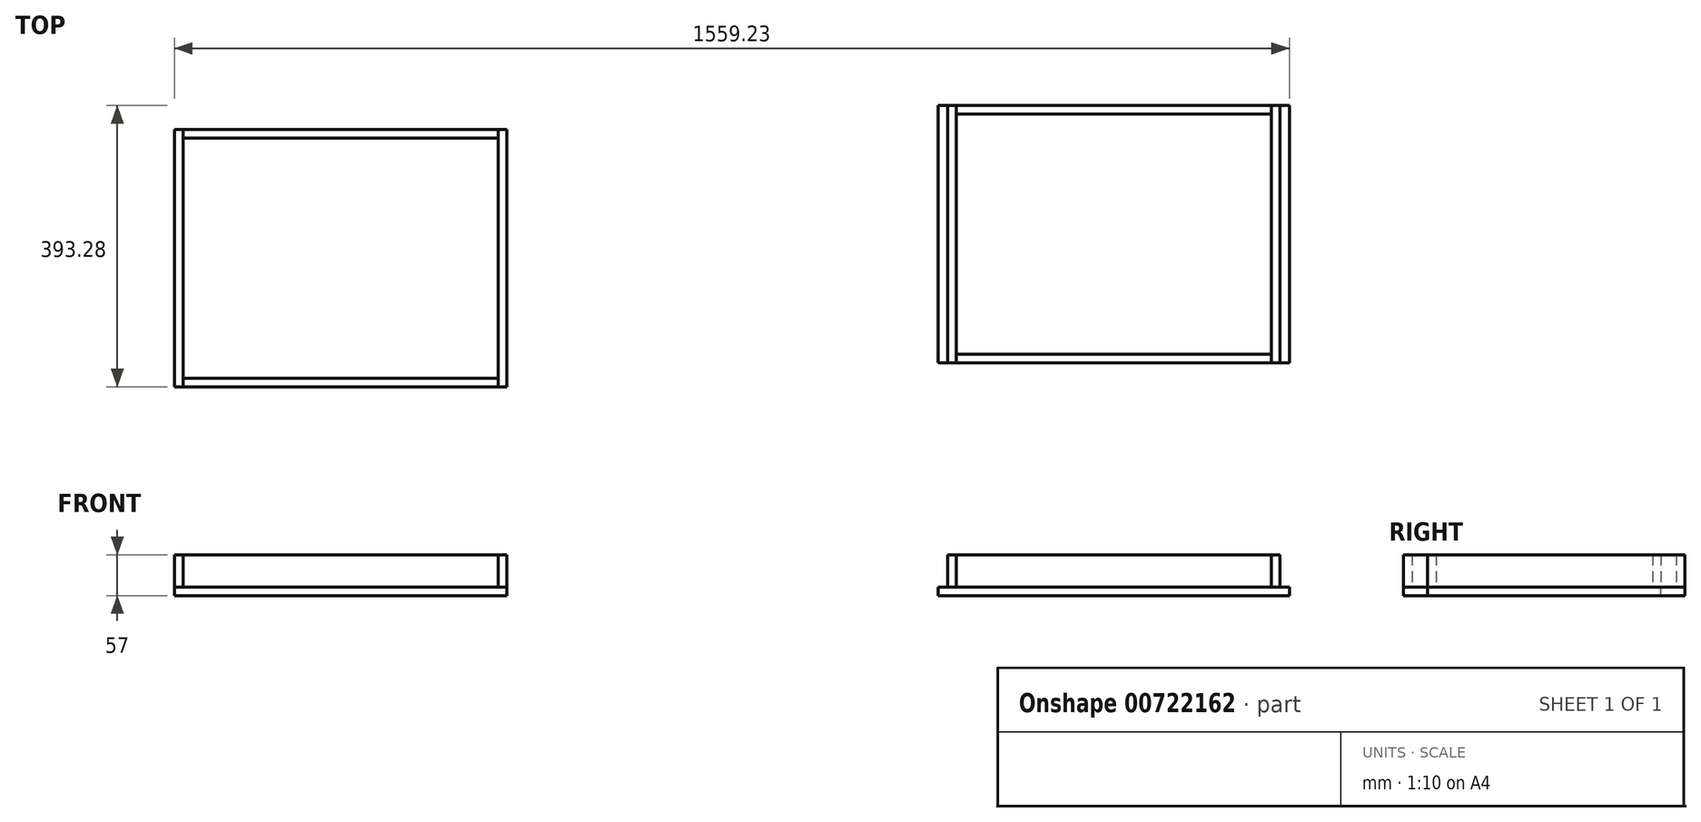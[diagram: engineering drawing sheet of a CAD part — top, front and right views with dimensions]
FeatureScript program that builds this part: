
annotation { "Feature Type Name" : "Feature", "Feature Type Description" : "" }
export const myFeature = defineFeature(function(context is Context, id is Id, definition is map)
    precondition{}
    {
        {
            var Q0;
            Q0=qCreatedBy(makeId("Top.planeOp"),FACE);
            var sketch = newSketch(context, id + "F0", { "sketchPlane" : qUnion([Q0])});
            skLineSegment(sketch, "E0.bottom", {"start": v(-232.5, -180) * mm, "end": v(232.5, -180) * mm});
            skLineSegment(sketch, "E0.top", {"start": v(-232.5, 180) * mm, "end": v(232.5, 180) * mm});
            skLineSegment(sketch, "E0.left", {"start": v(-232.5, -180) * mm, "end": v(-232.5, 180) * mm});
            skLineSegment(sketch, "E0.right", {"start": v(232.5, -180) * mm, "end": v(232.5, 180) * mm});
            skPoint(sketch, "E0.middle", {"position": v(0, 0) * mm});
            skLineSegment(sketch, "E1", {"start": v(-220.5, 180) * mm, "end": v(-220.5, -180) * mm});
            skLineSegment(sketch, "E2", {"start": v(220.5, 180) * mm, "end": v(220.5, -180) * mm});
            skLineSegment(sketch, "E3", {"start": v(-220.5, -168) * mm, "end": v(220.5, -168) * mm});
            skLineSegment(sketch, "E4", {"start": v(-220.5, 168) * mm, "end": v(220.5, 168) * mm});
            skLineSegment(sketch, "E5", {"start": v(-232.5, -180) * mm, "end": v(-245.5, -180) * mm});
            skLineSegment(sketch, "E6", {"start": v(-245.5, -180) * mm, "end": v(-245.5, 180) * mm});
            skLineSegment(sketch, "E7", {"start": v(-245.5, 180) * mm, "end": v(-232.5, 180) * mm});
            skLineSegment(sketch, "E8", {"start": v(232.5, 180) * mm, "end": v(245.5, 180) * mm});
            skLineSegment(sketch, "E9", {"start": v(245.5, 180) * mm, "end": v(245.5, -180) * mm});
            skLineSegment(sketch, "E10", {"start": v(245.5, -180) * mm, "end": v(232.5, -180) * mm});
            skSolve(sketch);
        }
        {
            var Q0;
            Q0 = qSketchRegion(id + "F0", true);
            var Q1;
            {var subQ0=sQuery(id+"F0.wireOp",EDGE,"E3");Q1=makeQuery(id+"F0.imprint","IMPRINT",FACE,{"disambiguationData":[TD([[makeQuery(id+"F0.imprint","IMPRINT",EDGE,{"derivedFrom":subQ0}),1.0]])]});}
            extrude(context, id + "F1", {"entities" : qUnion([Q0, Q1]), "oppositeDirection" : true, "depth" : 12 * mm, "offsetDistance" : 25 * mm});
        }
        {
            var Q0;
            {var subQ0=sQuery(id+"F0.wireOp",EDGE,"E0.left");Q0=makeQuery(id+"F0.imprint","IMPRINT",FACE,{"disambiguationData":[TD([[makeQuery(id+"F0.imprint","IMPRINT",EDGE,{"derivedFrom":subQ0}),-1.0]])]});}
            var Q1;
            {var subQ4=sQuery(id+"F0.wireOp",EDGE,"E0.right");Q1=makeQuery(id+"F0.imprint","IMPRINT",FACE,{"disambiguationData":[TD([[makeQuery(id+"F0.imprint","IMPRINT",EDGE,{"derivedFrom":subQ4}),1.0]])]});}
            extrude(context, id + "F2", {"entities" : qUnion([Q0, Q1]), "depth" : 45 * mm, "offsetDistance" : 25 * mm});
        }
        {
            var Q0;
            {var subQ5=sQuery(id+"F0.wireOp",EDGE,"E4");Q0=makeQuery(id+"F0.imprint","IMPRINT",FACE,{"disambiguationData":[TD([[makeQuery(id+"F0.imprint","IMPRINT",EDGE,{"derivedFrom":subQ5}),1.0]])]});}
            var Q1;
            {var subQ5=sQuery(id+"F0.wireOp",EDGE,"E3");Q1=makeQuery(id+"F0.imprint","IMPRINT",FACE,{"disambiguationData":[TD([[makeQuery(id+"F0.imprint","IMPRINT",EDGE,{"derivedFrom":subQ5}),-1.0]])]});}
            extrude(context, id + "F3", {"entities" : qUnion([Q0, Q1]), "depth" : 45 * mm, "offsetDistance" : 25 * mm});
        }
        {
            var Q0;
            Q0=qCreatedBy(makeId("Top.planeOp"),FACE);
            var sketch = newSketch(context, id + "F4", { "sketchPlane" : qUnion([Q0])});
            skLineSegment(sketch, "E11.bottom", {"start": v(-1313.73, -213.28) * mm, "end": v(-848.73, -213.28) * mm});
            skLineSegment(sketch, "E11.top", {"start": v(-1313.73, 146.72) * mm, "end": v(-848.73, 146.72) * mm});
            skLineSegment(sketch, "E11.left", {"start": v(-1313.73, -213.28) * mm, "end": v(-1313.73, 146.72) * mm});
            skLineSegment(sketch, "E11.right", {"start": v(-848.73, -213.28) * mm, "end": v(-848.73, 146.72) * mm});
            skPoint(sketch, "E11.middle", {"position": v(-1081.23, -33.28) * mm});
            skLineSegment(sketch, "E12", {"start": v(-1301.73, 146.72) * mm, "end": v(-1301.73, -213.28) * mm});
            skLineSegment(sketch, "E13", {"start": v(-860.73, 146.72) * mm, "end": v(-860.73, -213.28) * mm});
            skLineSegment(sketch, "E14", {"start": v(-1301.73, -201.28) * mm, "end": v(-860.73, -201.28) * mm});
            skLineSegment(sketch, "E15", {"start": v(-1301.73, 134.72) * mm, "end": v(-860.73, 134.72) * mm});
            skLineSegment(sketch, "E16", {"start": v(-1313.73, -213.28) * mm, "end": v(-1326.73, -213.28) * mm});
            skLineSegment(sketch, "E17", {"start": v(-1326.73, -213.28) * mm, "end": v(-1326.73, 146.72) * mm});
            skLineSegment(sketch, "E18", {"start": v(-1326.73, 146.72) * mm, "end": v(-1313.73, 146.72) * mm});
            skLineSegment(sketch, "E19", {"start": v(-848.73, 146.72) * mm, "end": v(-835.73, 146.72) * mm});
            skLineSegment(sketch, "E20", {"start": v(-835.73, 146.72) * mm, "end": v(-835.73, -213.28) * mm});
            skLineSegment(sketch, "E21", {"start": v(-835.73, -213.28) * mm, "end": v(-848.73, -213.28) * mm});
            skSolve(sketch);
        }
        {
            var Q0;
            {var subQ5=sQuery(id+"F4.wireOp",EDGE,"E14");Q0=makeQuery(id+"F4.imprint","IMPRINT",FACE,{"disambiguationData":[TD([[makeQuery(id+"F4.imprint","IMPRINT",EDGE,{"derivedFrom":subQ5}),-1.0]])]});}
            var Q1;
            {var subQ5=sQuery(id+"F4.wireOp",EDGE,"E15");Q1=makeQuery(id+"F4.imprint","IMPRINT",FACE,{"disambiguationData":[TD([[makeQuery(id+"F4.imprint","IMPRINT",EDGE,{"derivedFrom":subQ5}),1.0]])]});}
            var Q2;
            {var subQ0=sQuery(id+"F4.wireOp",EDGE,"E11.left");Q2=makeQuery(id+"F4.imprint","IMPRINT",FACE,{"disambiguationData":[TD([[makeQuery(id+"F4.imprint","IMPRINT",EDGE,{"derivedFrom":subQ0}),-1.0]])]});}
            var Q3;
            {var subQ4=sQuery(id+"F4.wireOp",EDGE,"E11.right");Q3=makeQuery(id+"F4.imprint","IMPRINT",FACE,{"disambiguationData":[TD([[makeQuery(id+"F4.imprint","IMPRINT",EDGE,{"derivedFrom":subQ4}),1.0]])]});}
            var Q4;
            {var subQ0=sQuery(id+"F4.wireOp",EDGE,"E14");Q4=makeQuery(id+"F4.imprint","IMPRINT",FACE,{"disambiguationData":[TD([[makeQuery(id+"F4.imprint","IMPRINT",EDGE,{"derivedFrom":subQ0}),1.0]])]});}
            extrude(context, id + "F5", {"entities" : qUnion([Q0, Q1, Q2, Q3, Q4]), "oppositeDirection" : true, "depth" : 12 * mm, "offsetDistance" : 25 * mm});
        }
        {
            var Q0;
            {var subQ4=sQuery(id+"F4.wireOp",EDGE,"E11.right");Q0=makeQuery(id+"F4.imprint","IMPRINT",FACE,{"disambiguationData":[TD([[makeQuery(id+"F4.imprint","IMPRINT",EDGE,{"derivedFrom":subQ4}),1.0]])]});}
            var Q1;
            {var subQ0=sQuery(id+"F4.wireOp",EDGE,"E11.left");Q1=makeQuery(id+"F4.imprint","IMPRINT",FACE,{"disambiguationData":[TD([[makeQuery(id+"F4.imprint","IMPRINT",EDGE,{"derivedFrom":subQ0}),-1.0]])]});}
            extrude(context, id + "F6", {"entities" : qUnion([Q0, Q1]), "depth" : 45 * mm, "offsetDistance" : 25 * mm});
        }
        {
            var Q0;
            {var subQ5=sQuery(id+"F4.wireOp",EDGE,"E15");Q0=makeQuery(id+"F4.imprint","IMPRINT",FACE,{"disambiguationData":[TD([[makeQuery(id+"F4.imprint","IMPRINT",EDGE,{"derivedFrom":subQ5}),1.0]])]});}
            var Q1;
            {var subQ5=sQuery(id+"F4.wireOp",EDGE,"E14");Q1=makeQuery(id+"F4.imprint","IMPRINT",FACE,{"disambiguationData":[TD([[makeQuery(id+"F4.imprint","IMPRINT",EDGE,{"derivedFrom":subQ5}),-1.0]])]});}
            extrude(context, id + "F7", {"entities" : qUnion([Q0, Q1]), "depth" : 45 * mm, "offsetDistance" : 25 * mm});
        }
    });
